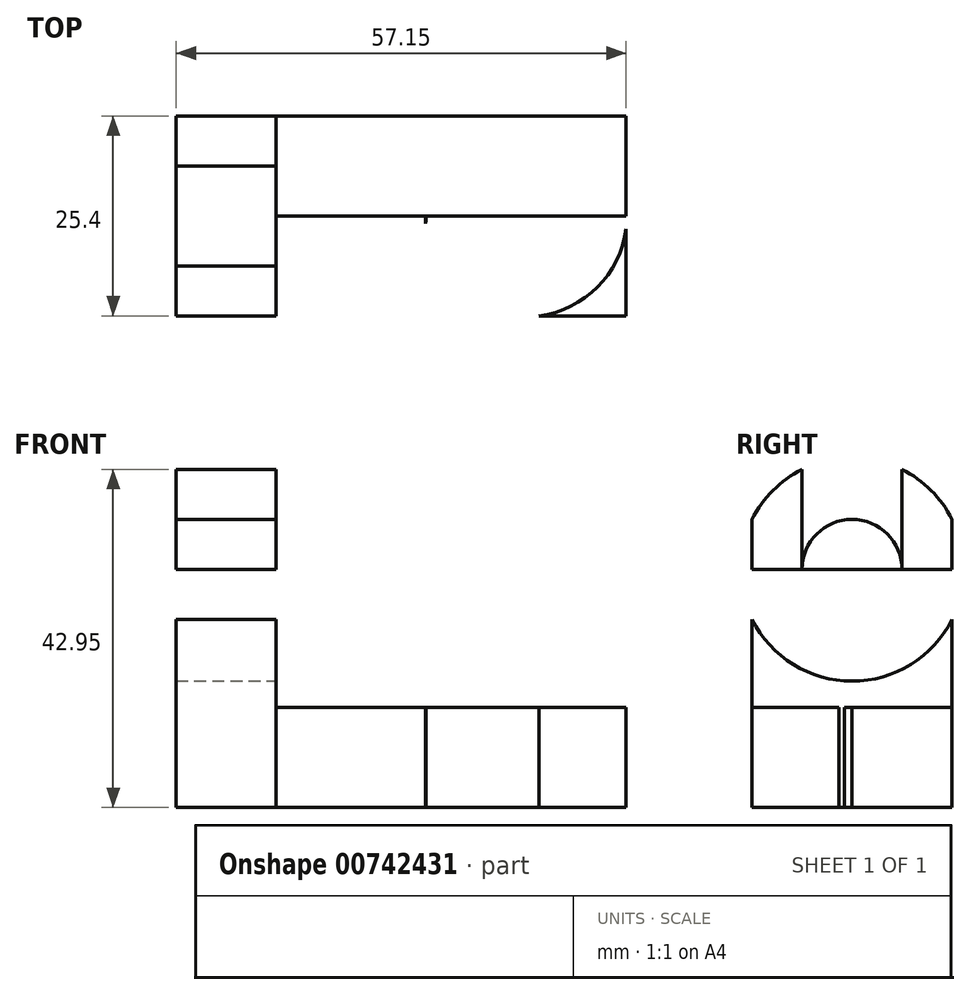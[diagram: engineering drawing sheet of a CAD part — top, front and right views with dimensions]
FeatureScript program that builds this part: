
annotation { "Feature Type Name" : "Feature", "Feature Type Description" : "" }
export const myFeature = defineFeature(function(context is Context, id is Id, definition is map)
    precondition{}
    {
        {
            var Q0;
            Q0=qCreatedBy(makeId("Front.planeOp"),FACE);
            var sketch = newSketch(context, id + "F0", { "sketchPlane" : qUnion([Q0])});
            skLineSegment(sketch, "E0", {"start": v(0, 0) * mm, "end": v(57.15, 0) * mm});
            skLineSegment(sketch, "E1", {"start": v(57.15, 0) * mm, "end": v(57.15, 44.45) * mm});
            skLineSegment(sketch, "E2", {"start": v(57.15, 44.45) * mm, "end": v(0, 44.45) * mm});
            skLineSegment(sketch, "E3", {"start": v(0, 44.45) * mm, "end": v(0, 0) * mm});
            skSolve(sketch);
        }
        {
            var Q0;
            Q0 = qSketchRegion(id + "F0", true);
            extrude(context, id + "F1", {"entities" : qUnion([Q0]), "depth" : 25.4 * mm, "offsetDistance" : 25.4 * mm});
        }
        {
            var Q0;
            Q0=makeQuery(id+"F1.opExtrude","CAP_FACE",FACE,{"disambiguationData":[OSD([sQuery(id+"F0.wireOp",EDGE,"E0"),sQuery(id+"F0.wireOp",EDGE,"E1"),sQuery(id+"F0.wireOp",EDGE,"E2"),sQuery(id+"F0.wireOp",EDGE,"E3")])],"isStart":false});
            var sketch = newSketch(context, id + "F2", { "sketchPlane" : qUnion([Q0])});
            skLineSegment(sketch, "E4", {"start": v(12.7, 44.45) * mm, "end": v(12.7, 12.7) * mm});
            skLineSegment(sketch, "E5", {"start": v(12.7, 12.7) * mm, "end": v(57.15, 12.7) * mm});
            skSolve(sketch);
        }
        {
            var Q0;
            {var subQ0=sQuery(id+"F2.wireOp",EDGE,"E4");Q0=makeQuery(id+"F2.imprint","IMPRINT",FACE,{"disambiguationData":[TD([[makeQuery(id+"F2.imprint","IMPRINT",EDGE,{"derivedFrom":subQ0}),1.0]])]});}
            extrude(context, id + "F3", {"entities" : qUnion([Q0]), "operationType" : NewBodyOperationType.REMOVE, "oppositeDirection" : true, "depth" : 25.4 * mm, "offsetDistance" : 25.4 * mm});
        }
        {
            var Q0;
            Q0=makeQuery(id+"F3.boolean.opBoolean","COPY",FACE,{"derivedFrom":makeQuery(id+"F3.opExtrude","SWEPT_FACE",FACE,{"disambiguationData":[OSD([sQuery(id+"F2.wireOp",EDGE,"E4")])]})});
            var sketch = newSketch(context, id + "F4", { "sketchPlane" : qUnion([Q0])});
            skLineSegment(sketch, "E6", {"start": v(-12.7, 44.45) * mm, "end": v(-12.7, 12.7) * mm});
            skLineSegment(sketch, "E7", {"start": v(-25.4, 30.25) * mm, "end": v(0, 30.25) * mm});
            skCircle(sketch, "E8", {"center": v(-12.7, 30.25) * mm, "radius": 14.2 * mm});
            skCircle(sketch, "E9", {"center": v(-12.7, 30.25) * mm, "radius": 6.35 * mm});
            skLineSegment(sketch, "E10", {"start": v(-19.05, 30.25) * mm, "end": v(-19.05, 42.95) * mm});
            skLineSegment(sketch, "E11", {"start": v(-6.35, 30.25) * mm, "end": v(-6.35, 42.95) * mm});
            skSolve(sketch);
        }
        {
            var Q0;
            {var subQ0=sQuery(id+"F4.wireOp",EDGE,"E8");var subQ4=makeQuery(id+"F4.imprint","INTERSECT",VERTEX,{"derivedFrom":[subQ0,sQuery(id+"F4.wireOp",EDGE,"E10")]});Q0=makeQuery(id+"F4.imprint","IMPRINT",FACE,{"disambiguationData":[TD([[makeQuery(id+"F4.imprint","IMPRINT",EDGE,{"disambiguationData":[TD([[subQ4,-1.0]])],"derivedFrom":subQ0}),-1.0]])]});}
            var Q1;
            {var subQ0=sQuery(id+"F4.wireOp",EDGE,"E8");var subQ1=makeQuery(id+"F4.imprint","INTERSECT",VERTEX,{"derivedFrom":[subQ0,sQuery(id+"F4.wireOp",EDGE,"E11")]});Q1=makeQuery(id+"F4.imprint","IMPRINT",FACE,{"disambiguationData":[TD([[makeQuery(id+"F4.imprint","IMPRINT",EDGE,{"disambiguationData":[TD([[subQ1,1.0]])],"derivedFrom":subQ0}),-1.0]])]});}
            var Q2;
            {var subQ5=sQuery(id+"F4.wireOp",EDGE,"E10");Q2=makeQuery(id+"F4.imprint","IMPRINT",FACE,{"disambiguationData":[TD([[makeQuery(id+"F4.imprint","IMPRINT",EDGE,{"derivedFrom":subQ5}),-1.0]])]});}
            var Q3;
            {var subQ5=sQuery(id+"F4.wireOp",EDGE,"E11");Q3=makeQuery(id+"F4.imprint","IMPRINT",FACE,{"disambiguationData":[TD([[makeQuery(id+"F4.imprint","IMPRINT",EDGE,{"derivedFrom":subQ5}),1.0]])]});}
            var Q4;
            {var subQ0=sQuery(id+"F4.wireOp",EDGE,"E7");var subQ1=sQuery(id+"F4.wireOp",EDGE,"E6");var subQ2=makeQuery(id+"F4.imprint","INTERSECT",VERTEX,{"derivedFrom":[subQ1,subQ0]});Q4=makeQuery(id+"F4.imprint","IMPRINT",FACE,{"disambiguationData":[TD([[makeQuery(id+"F4.imprint","IMPRINT",EDGE,{"disambiguationData":[TD([[subQ2,-1.0]])],"derivedFrom":subQ1}),-1.0]])]});}
            var Q5;
            {var subQ0=sQuery(id+"F4.wireOp",EDGE,"E9");var subQ1=sQuery(id+"F4.wireOp",EDGE,"E6");var subQ2=makeQuery(id+"F4.imprint","INTERSECT",VERTEX,{"disambiguationData":[OD(0.0)],"derivedFrom":[subQ1,subQ0]});Q5=makeQuery(id+"F4.imprint","IMPRINT",FACE,{"disambiguationData":[TD([[makeQuery(id+"F4.imprint","IMPRINT",EDGE,{"disambiguationData":[TD([[subQ2,-1.0]])],"derivedFrom":subQ1}),-1.0]])]});}
            var Q6;
            {var subQ0=sQuery(id+"F4.wireOp",EDGE,"E7");var subQ1=sQuery(id+"F4.wireOp",EDGE,"E6");var subQ2=makeQuery(id+"F4.imprint","INTERSECT",VERTEX,{"derivedFrom":[subQ1,subQ0]});Q6=makeQuery(id+"F4.imprint","IMPRINT",FACE,{"disambiguationData":[TD([[makeQuery(id+"F4.imprint","IMPRINT",EDGE,{"disambiguationData":[TD([[subQ2,-1.0]])],"derivedFrom":subQ1}),1.0]])]});}
            var Q7;
            {var subQ0=sQuery(id+"F4.wireOp",EDGE,"E9");var subQ1=sQuery(id+"F4.wireOp",EDGE,"E6");var subQ2=makeQuery(id+"F4.imprint","INTERSECT",VERTEX,{"disambiguationData":[OD(0.0)],"derivedFrom":[subQ1,subQ0]});Q7=makeQuery(id+"F4.imprint","IMPRINT",FACE,{"disambiguationData":[TD([[makeQuery(id+"F4.imprint","IMPRINT",EDGE,{"disambiguationData":[TD([[subQ2,-1.0]])],"derivedFrom":subQ1}),1.0]])]});}
            extrude(context, id + "F5", {"entities" : qUnion([Q0, Q1, Q2, Q3, Q4, Q5, Q6, Q7]), "operationType" : NewBodyOperationType.REMOVE, "oppositeDirection" : true, "depth" : 25.4 * mm, "offsetDistance" : 25.4 * mm});
        }
        {
            var Q0;
            Q0=makeQuery(id+"F3.boolean.opBoolean","COPY",FACE,{"derivedFrom":makeQuery(id+"F3.opExtrude","SWEPT_FACE",FACE,{"disambiguationData":[OSD([sQuery(id+"F2.wireOp",EDGE,"E5")])]})});
            var sketch = newSketch(context, id + "F6", { "sketchPlane" : qUnion([Q0])});
            skLineSegment(sketch, "E12", {"start": v(25.4, 0) * mm, "end": v(25.4, -25.4) * mm});
            skLineSegment(sketch, "E13", {"start": v(44.45, 0) * mm, "end": v(44.45, -25.4) * mm});
            skLineSegment(sketch, "E14", {"start": v(12.7, -12.7) * mm, "end": v(57.15, -12.7) * mm});
            skCircle(sketch, "E15", {"center": v(25.4, -12.7) * mm, "radius": 6.35 * mm});
            skCircle(sketch, "E16", {"center": v(44.45, -12.7) * mm, "radius": 6.35 * mm});
            skCircle(sketch, "E17", {"center": v(44.45, -12.7) * mm, "radius": 12.8 * mm});
            skSolve(sketch);
        }
        {
            var Q0;
            {var subQ0=sQuery(id+"F6.wireOp",EDGE,"E14");var subQ1=sQuery(id+"F6.wireOp",EDGE,"E12");var subQ2=makeQuery(id+"F6.imprint","INTERSECT",VERTEX,{"derivedFrom":[subQ1,subQ0]});Q0=makeQuery(id+"F6.imprint","IMPRINT",FACE,{"disambiguationData":[TD([[makeQuery(id+"F6.imprint","IMPRINT",EDGE,{"disambiguationData":[TD([[subQ2,-1.0]])],"derivedFrom":subQ1}),-1.0]])]});}
            var Q1;
            {var subQ0=sQuery(id+"F6.wireOp",EDGE,"E15");var subQ1=sQuery(id+"F6.wireOp",EDGE,"E12");var subQ2=makeQuery(id+"F6.imprint","INTERSECT",VERTEX,{"disambiguationData":[OD(0.0)],"derivedFrom":[subQ1,subQ0]});Q1=makeQuery(id+"F6.imprint","IMPRINT",FACE,{"disambiguationData":[TD([[makeQuery(id+"F6.imprint","IMPRINT",EDGE,{"disambiguationData":[TD([[subQ2,-1.0]])],"derivedFrom":subQ1}),-1.0]])]});}
            var Q2;
            {var subQ0=sQuery(id+"F6.wireOp",EDGE,"E15");var subQ1=sQuery(id+"F6.wireOp",EDGE,"E12");var subQ2=makeQuery(id+"F6.imprint","INTERSECT",VERTEX,{"disambiguationData":[OD(0.0)],"derivedFrom":[subQ1,subQ0]});Q2=makeQuery(id+"F6.imprint","IMPRINT",FACE,{"disambiguationData":[TD([[makeQuery(id+"F6.imprint","IMPRINT",EDGE,{"disambiguationData":[TD([[subQ2,-1.0]])],"derivedFrom":subQ1}),1.0]])]});}
            var Q3;
            {var subQ0=sQuery(id+"F6.wireOp",EDGE,"E14");var subQ1=sQuery(id+"F6.wireOp",EDGE,"E12");var subQ2=makeQuery(id+"F6.imprint","INTERSECT",VERTEX,{"derivedFrom":[subQ1,subQ0]});Q3=makeQuery(id+"F6.imprint","IMPRINT",FACE,{"disambiguationData":[TD([[makeQuery(id+"F6.imprint","IMPRINT",EDGE,{"disambiguationData":[TD([[subQ2,-1.0]])],"derivedFrom":subQ1}),1.0]])]});}
            var Q4;
            {var subQ0=sQuery(id+"F6.wireOp",EDGE,"E16");var subQ1=sQuery(id+"F6.wireOp",EDGE,"E13");var subQ2=makeQuery(id+"F6.imprint","INTERSECT",VERTEX,{"disambiguationData":[OD(0.0)],"derivedFrom":[subQ1,subQ0]});Q4=makeQuery(id+"F6.imprint","IMPRINT",FACE,{"disambiguationData":[TD([[makeQuery(id+"F6.imprint","IMPRINT",EDGE,{"disambiguationData":[TD([[subQ2,-1.0]])],"derivedFrom":subQ1}),1.0]])]});}
            var Q5;
            {var subQ0=sQuery(id+"F6.wireOp",EDGE,"E16");var subQ1=sQuery(id+"F6.wireOp",EDGE,"E13");var subQ2=makeQuery(id+"F6.imprint","INTERSECT",VERTEX,{"disambiguationData":[OD(0.0)],"derivedFrom":[subQ1,subQ0]});Q5=makeQuery(id+"F6.imprint","IMPRINT",FACE,{"disambiguationData":[TD([[makeQuery(id+"F6.imprint","IMPRINT",EDGE,{"disambiguationData":[TD([[subQ2,-1.0]])],"derivedFrom":subQ1}),-1.0]])]});}
            var Q6;
            {var subQ0=sQuery(id+"F6.wireOp",EDGE,"E14");var subQ1=sQuery(id+"F6.wireOp",EDGE,"E13");var subQ2=makeQuery(id+"F6.imprint","INTERSECT",VERTEX,{"derivedFrom":[subQ1,subQ0]});Q6=makeQuery(id+"F6.imprint","IMPRINT",FACE,{"disambiguationData":[TD([[makeQuery(id+"F6.imprint","IMPRINT",EDGE,{"disambiguationData":[TD([[subQ2,-1.0]])],"derivedFrom":subQ1}),-1.0]])]});}
            var Q7;
            {var subQ0=sQuery(id+"F6.wireOp",EDGE,"E14");var subQ1=sQuery(id+"F6.wireOp",EDGE,"E13");var subQ2=makeQuery(id+"F6.imprint","INTERSECT",VERTEX,{"derivedFrom":[subQ1,subQ0]});Q7=makeQuery(id+"F6.imprint","IMPRINT",FACE,{"disambiguationData":[TD([[makeQuery(id+"F6.imprint","IMPRINT",EDGE,{"disambiguationData":[TD([[subQ2,-1.0]])],"derivedFrom":subQ1}),1.0]])]});}
            var Q8;
            {var subQ0=sQuery(id+"F6.wireOp",EDGE,"E17");var subQ1=sQuery(id+"F2.wireOp",EDGE,"E5");var subQ2=makeQuery(id+"F3.boolean.opBoolean","COPY",EDGE,{"derivedFrom":makeQuery(id+"F3.opExtrude","CAP_EDGE",EDGE,{"disambiguationData":[OSD([subQ1])],"isStart":false})});var subQ3=makeQuery(id+"F6.imprint","INTERSECT",VERTEX,{"disambiguationData":[OD(0.0)],"derivedFrom":[subQ2,subQ0]});Q8=makeQuery(id+"F6.imprint","IMPRINT",FACE,{"disambiguationData":[TD([[makeQuery(id+"F6.imprint","IMPRINT",EDGE,{"disambiguationData":[TD([[subQ3,1.0]])],"derivedFrom":subQ0}),-1.0]])]});}
            var Q9;
            {var subQ0=sQuery(id+"F6.wireOp",EDGE,"E17");var subQ1=sQuery(id+"F2.wireOp",EDGE,"E5");var subQ2=makeQuery(id+"F3.boolean.opBoolean","COPY",EDGE,{"derivedFrom":makeQuery(id+"F3.opExtrude","CAP_EDGE",EDGE,{"disambiguationData":[OSD([subQ1])],"isStart":true})});var subQ3=makeQuery(id+"F6.imprint","INTERSECT",VERTEX,{"disambiguationData":[OD(1.0)],"derivedFrom":[subQ2,subQ0]});Q9=makeQuery(id+"F6.imprint","IMPRINT",FACE,{"disambiguationData":[TD([[makeQuery(id+"F6.imprint","IMPRINT",EDGE,{"disambiguationData":[TD([[subQ3,-1.0]])],"derivedFrom":subQ0}),-1.0]])]});}
            extrude(context, id + "F7", {"entities" : qUnion([Q0, Q1, Q2, Q3, Q4, Q5, Q6, Q7, Q8, Q9]), "operationType" : NewBodyOperationType.REMOVE, "oppositeDirection" : true, "depth" : 25.4 * mm, "offsetDistance" : 25.4 * mm});
        }
    });
